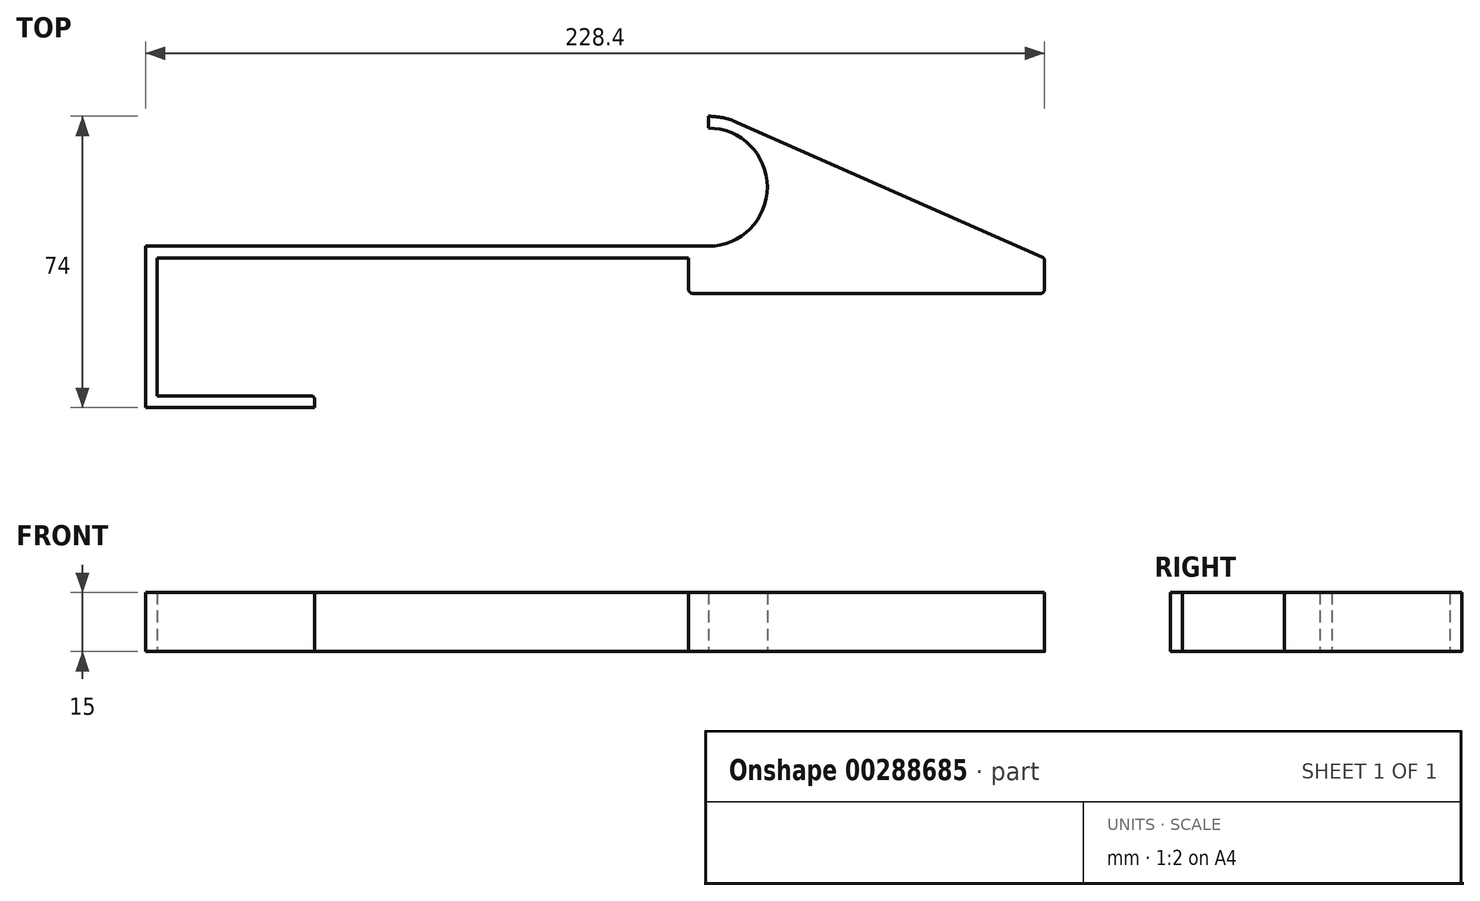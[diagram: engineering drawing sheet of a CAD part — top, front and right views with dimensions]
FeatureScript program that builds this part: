
annotation { "Feature Type Name" : "Feature", "Feature Type Description" : "" }
export const myFeature = defineFeature(function(context is Context, id is Id, definition is map)
    precondition{}
    {
        {
            var Q0;
            Q0=qCreatedBy(makeId("Top.planeOp"),FACE);
            var sketch = newSketch(context, id + "F0", { "sketchPlane" : qUnion([Q0])});
            skLineSegment(sketch, "E0", {"start": v(-70, 0) * mm, "end": v(65, 0) * mm});
            skLineSegment(sketch, "E1", {"start": v(-70, 0) * mm, "end": v(-70, -35) * mm});
            skLineSegment(sketch, "E2", {"start": v(-70, -35) * mm, "end": v(-30, -35) * mm});
            skLineSegment(sketch, "E3", {"start": v(-30, -35) * mm, "end": v(-30, -38) * mm});
            skLineSegment(sketch, "E4", {"start": v(-30, -38) * mm, "end": v(-73, -38) * mm});
            skLineSegment(sketch, "E5", {"start": v(-73, -38) * mm, "end": v(-73, 3) * mm});
            skLineSegment(sketch, "E6", {"start": v(-73, 3) * mm, "end": v(70, 3) * mm});
            skArc(sketch, "E7", {"start": v(70, 3) * mm, "mid": v(85, 18) * mm, "end": v(70, 33) * mm});
            skPoint(sketch, "E7.third.point", {"position": v(70, 3) * mm});
            skArc(sketch, "E8", {"start": v(60.05, 3) * mm, "mid": v(87.23, 12.8) * mm, "end": v(70, 36) * mm});
            skLineSegment(sketch, "E9", {"start": v(70, 33) * mm, "end": v(70, 36) * mm});
            skLineSegment(sketch, "E10", {"start": v(155.4, -9) * mm, "end": v(155.4, 0) * mm});
            skLineSegment(sketch, "E11", {"start": v(155.4, -9) * mm, "end": v(65, -9) * mm});
            skPoint(sketch, "E12.orphan", {"position": v(70, 0) * mm});
            skLineSegment(sketch, "E13", {"start": v(155.4, 0) * mm, "end": v(77.26, 34.47) * mm});
            skLineSegment(sketch, "E14", {"start": v(65, 0) * mm, "end": v(65, -9) * mm});
            skSolve(sketch);
        }
        {
            var Q0;
            Q0=makeQuery(id+"F0.imprint","IMPRINT",FACE,{"disambiguationData":[TD([[makeQuery(id+"F0.imprint","IMPRINT",EDGE,{"derivedFrom":sQuery(id+"F0.wireOp",EDGE,"E0")}),1.0]])]});
            var Q1;
            {var subQ5=sQuery(id+"F0.wireOp",EDGE,"E7");Q1=makeQuery(id+"F0.imprint","IMPRINT",FACE,{"disambiguationData":[TD([[makeQuery(id+"F0.imprint","IMPRINT",EDGE,{"derivedFrom":subQ5}),-1.0]])]});}
            extrude(context, id + "F1", {"entities" : qUnion([Q0, Q1]), "depth" : 15 * mm});
        }
        {
            var Q0;
            Q0=makeQuery(id+"F1.opExtrude","SWEPT_EDGE",EDGE,{"disambiguationData":[OSD([sQuery(id+"F0.wireOp",EDGE,"E11"),sQuery(id+"F0.wireOp",EDGE,"E14")])]});
            var Q1;
            Q1=makeQuery(id+"F1.opExtrude","SWEPT_EDGE",EDGE,{"disambiguationData":[OSD([sQuery(id+"F0.wireOp",EDGE,"E10"),sQuery(id+"F0.wireOp",EDGE,"E11")])]});
            var Q2;
            Q2=makeQuery(id+"F1.opExtrude","SWEPT_EDGE",EDGE,{"disambiguationData":[OSD([sQuery(id+"F0.wireOp",EDGE,"E10"),sQuery(id+"F0.wireOp",EDGE,"E13")])]});
            var Q3;
            Q3=makeQuery(id+"F1.opExtrude","SWEPT_EDGE",EDGE,{"disambiguationData":[OSD([sQuery(id+"F0.wireOp",EDGE,"E2"),sQuery(id+"F0.wireOp",EDGE,"E3")])]});
            fillet(context, id + "F2", {"entities" : qUnion([Q0, Q1, Q2, Q3]), "radius" : 1 * mm, "tangentPropagation" : true, "allowEdgeOverflow" : false});
        }
    });
